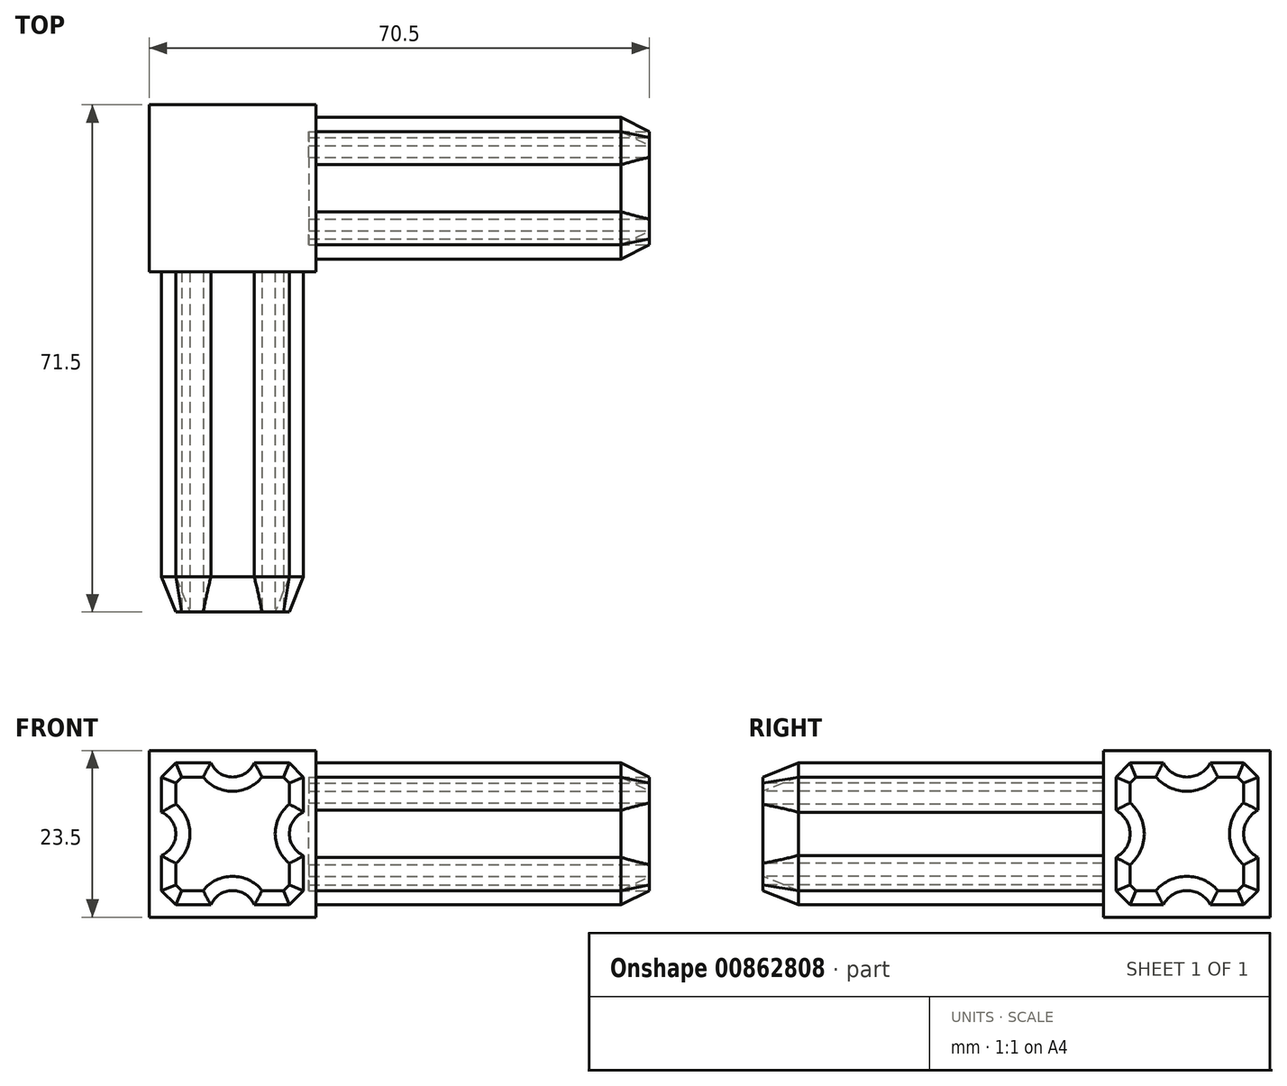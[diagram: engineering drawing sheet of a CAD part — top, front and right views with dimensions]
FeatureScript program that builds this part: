
annotation { "Feature Type Name" : "Feature", "Feature Type Description" : "" }
export const myFeature = defineFeature(function(context is Context, id is Id, definition is map)
    precondition{}
    {
        {
            var Q0;
            Q0=qCreatedBy(makeId("Top.planeOp"),FACE);
            var sketch = newSketch(context, id + "F0", { "sketchPlane" : qUnion([Q0])});
            skLineSegment(sketch, "E0.bottom", {"start": v(11.75, -11.75) * mm, "end": v(-11.75, -11.75) * mm});
            skLineSegment(sketch, "E0.top", {"start": v(11.75, 11.75) * mm, "end": v(-11.75, 11.75) * mm});
            skLineSegment(sketch, "E0.left", {"start": v(11.75, -11.75) * mm, "end": v(11.75, 11.75) * mm});
            skLineSegment(sketch, "E0.right", {"start": v(-11.75, -11.75) * mm, "end": v(-11.75, 11.75) * mm});
            skPoint(sketch, "E0.middle", {"position": v(0, 0) * mm});
            skSolve(sketch);
        }
        {
            var Q0;
            Q0=qSketchRegion(id+"F0",true);
            extrude(context, id + "F1", {"entities" : qUnion([Q0]), "endBound" : BoundingType.SYMMETRIC, "depth" : 23.5 * mm, "offsetDistance" : 25.4 * mm});
        }
        {
            var Q0;
            Q0=makeQuery(id+"F1.opExtrude","SWEPT_FACE",FACE,{"disambiguationData":[OSD([sQuery(id+"F0.wireOp",EDGE,"E0.left")])]});
            var sketch = newSketch(context, id + "F2", { "sketchPlane" : qUnion([Q0])});
            skLineSegment(sketch, "E1.bottom", {"start": v(10, -10) * mm, "end": v(-10, -10) * mm});
            skLineSegment(sketch, "E1.top", {"start": v(10, 10) * mm, "end": v(-10, 10) * mm});
            skLineSegment(sketch, "E1.left", {"start": v(10, -10) * mm, "end": v(10, 10) * mm});
            skLineSegment(sketch, "E1.right", {"start": v(-10, -10) * mm, "end": v(-10, 10) * mm});
            skPoint(sketch, "E1.middle", {"position": v(0, 0) * mm});
            skSolve(sketch);
        }
        {
            var Q0;
            Q0=qSketchRegion(id+"F2",true);
            extrude(context, id + "F3", {"entities" : qUnion([Q0]), "operationType" : NewBodyOperationType.ADD, "depth" : 47 * mm, "offsetDistance" : 25 * mm});
        }
        {
            var Q0;
            Q0=makeQuery(id+"F3.opExtrude","SWEPT_EDGE",EDGE,{"disambiguationData":[OSD([sQuery(id+"F2.wireOp",EDGE,"E1.top"),sQuery(id+"F2.wireOp",EDGE,"E1.right")])]});
            var Q1;
            Q1=makeQuery(id+"F3.opExtrude","SWEPT_EDGE",EDGE,{"disambiguationData":[OSD([sQuery(id+"F2.wireOp",EDGE,"E1.bottom"),sQuery(id+"F2.wireOp",EDGE,"E1.right")])]});
            var Q2;
            Q2=makeQuery(id+"F3.opExtrude","SWEPT_EDGE",EDGE,{"disambiguationData":[OSD([sQuery(id+"F2.wireOp",EDGE,"E1.top"),sQuery(id+"F2.wireOp",EDGE,"E1.left")])]});
            var Q3;
            Q3=makeQuery(id+"F3.opExtrude","SWEPT_EDGE",EDGE,{"disambiguationData":[OSD([sQuery(id+"F2.wireOp",EDGE,"E1.bottom"),sQuery(id+"F2.wireOp",EDGE,"E1.left")])]});
            chamfer(context, id + "F4", {"entities" : qUnion([Q0, Q1, Q2, Q3]), "width" : 2 * mm, "tangentPropagation" : true});
        }
        {
            var Q0;
            Q0=makeQuery(id+"F3.opExtrude","CAP_FACE",FACE,{"disambiguationData":[OSD([sQuery(id+"F2.wireOp",EDGE,"E1.bottom"),sQuery(id+"F2.wireOp",EDGE,"E1.top"),sQuery(id+"F2.wireOp",EDGE,"E1.left"),sQuery(id+"F2.wireOp",EDGE,"E1.right")])],"isStart":false});
            var sketch = newSketch(context, id + "F5", { "sketchPlane" : qUnion([Q0])});
            skCircle(sketch, "E2", {"center": v(0, 11.75) * mm, "radius": 3.75 * mm});
            skCircle(sketch, "E3.1.0", {"center": v(11.75, 0) * mm, "radius": 3.75 * mm});
            skCircle(sketch, "E3.2.0", {"center": v(0, -11.75) * mm, "radius": 3.75 * mm});
            skCircle(sketch, "E3.3.0", {"center": v(-11.75, 0) * mm, "radius": 3.75 * mm});
            skPoint(sketch, "E3.center", {"position": v(0, 0) * mm});
            skLineSegment(sketch, "E3.anchor1", {"start": v(0, 0) * mm, "end": v(0, 11.75) * mm, "construction": true});
            skLineSegment(sketch, "E3.anchor2", {"start": v(0, 0) * mm, "end": v(-11.75, 0) * mm, "construction": true});
            skSolve(sketch);
        }
        {
            var Q0;
            Q0=qSketchRegion(id+"F5",true);
            var Q1;
            Q1=makeQuery(id+"F1.opExtrude","SWEPT_FACE",FACE,{"disambiguationData":[OSD([sQuery(id+"F0.wireOp",EDGE,"E0.left")])]});
            extrude(context, id + "F6", {"entities" : qUnion([Q0]), "operationType" : NewBodyOperationType.REMOVE, "endBound" : BoundingType.UP_TO_SURFACE, "oppositeDirection" : true, "depth" : 25 * mm, "endBoundEntityFace" : qUnion([Q1]), "offsetDistance" : 25 * mm});
        }
        {
            var Q0;
            Q0=makeQuery(id+"F3.opExtrude","CAP_FACE",FACE,{"disambiguationData":[OSD([sQuery(id+"F2.wireOp",EDGE,"E1.bottom"),sQuery(id+"F2.wireOp",EDGE,"E1.top"),sQuery(id+"F2.wireOp",EDGE,"E1.left"),sQuery(id+"F2.wireOp",EDGE,"E1.right")])],"isStart":false});
            chamfer(context, id + "F7", {"entities" : qUnion([Q0]), "chamferType" : ChamferType.TWO_OFFSETS, "width1" : 2 * mm, "oppositeDirection" : false, "width2" : 4 * mm, "tangentPropagation" : true});
        }
        {
            var Q0;
            Q0=makeQuery(id+"F1.opExtrude","SWEPT_FACE",FACE,{"disambiguationData":[OSD([sQuery(id+"F0.wireOp",EDGE,"E0.bottom")])]});
            var sketch = newSketch(context, id + "F8", { "sketchPlane" : qUnion([Q0])});
            skLineSegment(sketch, "E4.bottom", {"start": v(10, -10) * mm, "end": v(-10, -10) * mm});
            skLineSegment(sketch, "E4.top", {"start": v(10, 10) * mm, "end": v(-10, 10) * mm});
            skLineSegment(sketch, "E4.left", {"start": v(10, -10) * mm, "end": v(10, 10) * mm});
            skLineSegment(sketch, "E4.right", {"start": v(-10, -10) * mm, "end": v(-10, 10) * mm});
            skPoint(sketch, "E4.middle", {"position": v(0, 0) * mm});
            skSolve(sketch);
        }
        {
            var Q0;
            Q0=makeQuery(id+"F8.imprint","IMPRINT",FACE,{"disambiguationData":[TD([[makeQuery(id+"F8.imprint","IMPRINT",EDGE,{"derivedFrom":sQuery(id+"F8.wireOp",EDGE,"E4.bottom")}),-1.0]])]});
            extrude(context, id + "F9", {"entities" : qUnion([Q0]), "operationType" : NewBodyOperationType.ADD, "depth" : 48 * mm, "offsetDistance" : 25 * mm});
        }
        {
            var Q0;
            Q0=makeQuery(id+"F9.opExtrude","CAP_FACE",FACE,{"disambiguationData":[OSD([sQuery(id+"F8.wireOp",EDGE,"E4.bottom"),sQuery(id+"F8.wireOp",EDGE,"E4.top"),sQuery(id+"F8.wireOp",EDGE,"E4.left"),sQuery(id+"F8.wireOp",EDGE,"E4.right")])],"isStart":false});
            var sketch = newSketch(context, id + "F10", { "sketchPlane" : qUnion([Q0])});
            skCircle(sketch, "E5", {"center": v(11.32, 0) * mm, "radius": 3.32 * mm});
            skPoint(sketch, "E5.centerSnap0", {"position": v(10, 0) * mm});
            skCircle(sketch, "E6.1.0", {"center": v(0, 11.32) * mm, "radius": 3.32 * mm});
            skCircle(sketch, "E6.2.0", {"center": v(-11.32, 0) * mm, "radius": 3.32 * mm});
            skCircle(sketch, "E6.3.0", {"center": v(0, -11.32) * mm, "radius": 3.32 * mm});
            skPoint(sketch, "E6.center", {"position": v(0, 0) * mm});
            skSolve(sketch);
        }
        {
            var Q0;
            Q0=qSketchRegion(id+"F10",true);
            var Q1;
            Q1=makeQuery(id+"F1.opExtrude","SWEPT_FACE",FACE,{"disambiguationData":[OSD([sQuery(id+"F0.wireOp",EDGE,"E0.bottom")])]});
            extrude(context, id + "F11", {"entities" : qUnion([Q0]), "operationType" : NewBodyOperationType.REMOVE, "oppositeDirection" : true, "depth" : 48 * mm, "endBoundEntityFace" : qUnion([Q1]), "offsetDistance" : 25 * mm});
        }
        {
            var Q0;
            Q0=makeQuery(id+"F9.opExtrude","SWEPT_EDGE",EDGE,{"disambiguationData":[OSD([sQuery(id+"F8.wireOp",EDGE,"E4.top"),sQuery(id+"F8.wireOp",EDGE,"E4.left")])]});
            var Q1;
            Q1=makeQuery(id+"F9.opExtrude","SWEPT_EDGE",EDGE,{"disambiguationData":[OSD([sQuery(id+"F8.wireOp",EDGE,"E4.bottom"),sQuery(id+"F8.wireOp",EDGE,"E4.left")])]});
            var Q2;
            Q2=makeQuery(id+"F9.opExtrude","SWEPT_EDGE",EDGE,{"disambiguationData":[OSD([sQuery(id+"F8.wireOp",EDGE,"E4.top"),sQuery(id+"F8.wireOp",EDGE,"E4.right")])]});
            var Q3;
            Q3=makeQuery(id+"F9.opExtrude","SWEPT_EDGE",EDGE,{"disambiguationData":[OSD([sQuery(id+"F8.wireOp",EDGE,"E4.bottom"),sQuery(id+"F8.wireOp",EDGE,"E4.right")])]});
            chamfer(context, id + "F12", {"entities" : qUnion([Q0, Q1, Q2, Q3]), "width" : 2 * mm, "tangentPropagation" : true});
        }
        {
            var Q0;
            Q0=makeQuery(id+"F9.opExtrude","CAP_FACE",FACE,{"disambiguationData":[OSD([sQuery(id+"F8.wireOp",EDGE,"E4.bottom"),sQuery(id+"F8.wireOp",EDGE,"E4.top"),sQuery(id+"F8.wireOp",EDGE,"E4.left"),sQuery(id+"F8.wireOp",EDGE,"E4.right")])],"isStart":false});
            chamfer(context, id + "F13", {"entities" : qUnion([Q0]), "chamferType" : ChamferType.TWO_OFFSETS, "width1" : 2 * mm, "oppositeDirection" : true, "width2" : 5 * mm, "tangentPropagation" : true});
        }
        {
            var Q0;
            Q0=makeQuery(id+"F3.opExtrude","CAP_FACE",FACE,{"disambiguationData":[OSD([sQuery(id+"F2.wireOp",EDGE,"E1.bottom"),sQuery(id+"F2.wireOp",EDGE,"E1.top"),sQuery(id+"F2.wireOp",EDGE,"E1.left"),sQuery(id+"F2.wireOp",EDGE,"E1.right")])],"isStart":false});
            extrude(context, id + "F14", {"entities" : qUnion([Q0]), "operationType" : NewBodyOperationType.REMOVE, "oppositeDirection" : true, "depth" : 48 * mm, "offsetDistance" : 25 * mm});
        }
        {
            var Q0;
            Q0=makeQuery(id+"F9.opExtrude","CAP_FACE",FACE,{"disambiguationData":[OSD([sQuery(id+"F8.wireOp",EDGE,"E4.bottom"),sQuery(id+"F8.wireOp",EDGE,"E4.top"),sQuery(id+"F8.wireOp",EDGE,"E4.left"),sQuery(id+"F8.wireOp",EDGE,"E4.right")])],"isStart":false});
            extrude(context, id + "F15", {"entities" : qUnion([Q0]), "operationType" : NewBodyOperationType.REMOVE, "oppositeDirection" : true, "depth" : 48 * mm, "offsetDistance" : 25 * mm});
        }
    });
